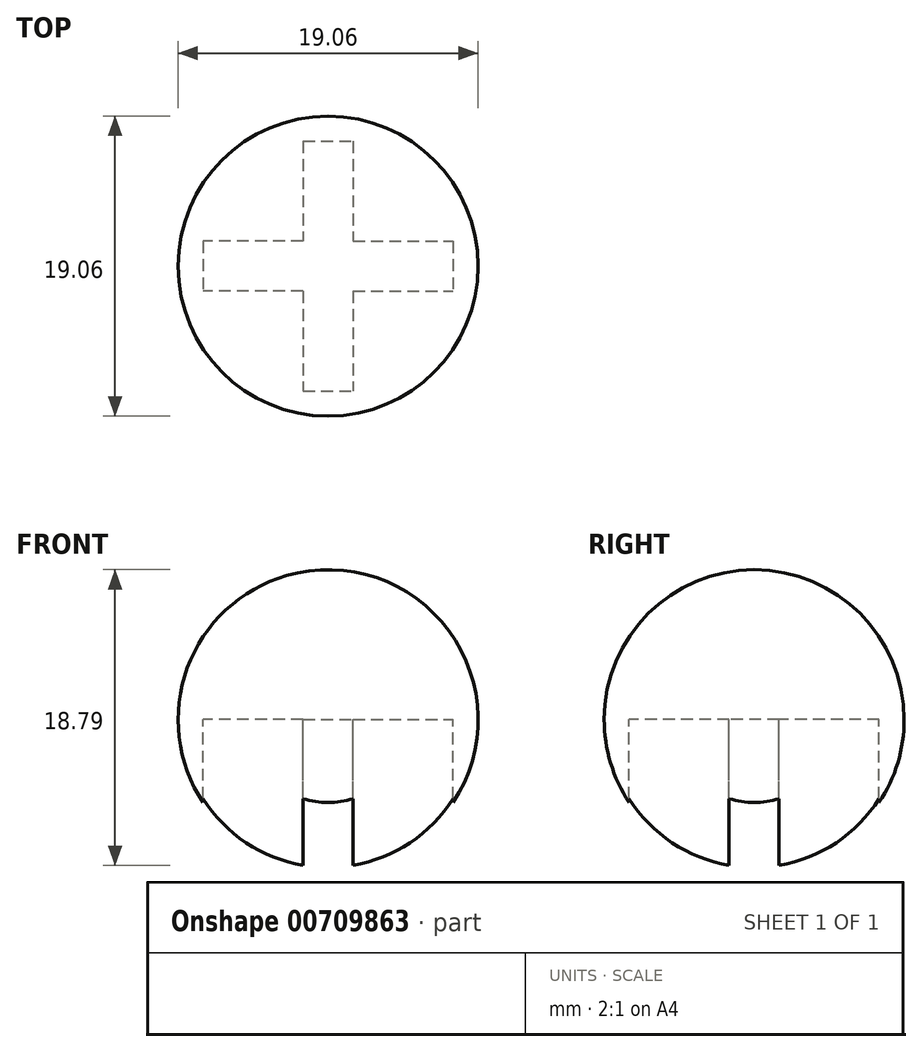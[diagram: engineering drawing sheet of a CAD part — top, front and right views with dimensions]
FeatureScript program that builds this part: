
annotation { "Feature Type Name" : "Feature", "Feature Type Description" : "" }
export const myFeature = defineFeature(function(context is Context, id is Id, definition is map)
    precondition{}
    {
        {
            var Q0;
            Q0=qCreatedBy(makeId("Top.planeOp"),FACE);
            var sketch = newSketch(context, id + "F0", { "sketchPlane" : qUnion([Q0])});
            skLineSegment(sketch, "E0", {"start": v(0, 9.53) * mm, "end": v(0, -9.53) * mm});
            skArc(sketch, "E1", {"start": v(0, -9.53) * mm, "mid": v(9.53, 0) * mm, "end": v(0, 9.53) * mm});
            skSolve(sketch);
        }
        {
            var Q0;
            Q0 = qSketchRegion(id + "F0", true);
            var Q1;
            Q1=sQuery(id+"F0.wireOp",EDGE,"E0");
            revolve(context, id + "F1", {"surfaceOperationType" : NewSurfaceOperationType.NEW, "entities" : qUnion([Q0]), "axis" : qUnion([Q1]), "revolveType" : RevolveType.FULL});
        }
        {
            var Q0;
            Q0=qCreatedBy(makeId("Top.planeOp"),FACE);
            var sketch = newSketch(context, id + "F2", { "sketchPlane" : qUnion([Q0])});
            skLineSegment(sketch, "E2.bottom", {"start": v(-1.59, 7.94) * mm, "end": v(1.59, 7.94) * mm});
            skLineSegment(sketch, "E2.top", {"start": v(-1.59, 1.59) * mm, "end": v(1.59, 1.59) * mm});
            skLineSegment(sketch, "E2.left", {"start": v(-1.59, 7.94) * mm, "end": v(-1.59, 1.59) * mm});
            skLineSegment(sketch, "E2.right", {"start": v(1.59, 7.94) * mm, "end": v(1.59, 1.59) * mm});
            skLineSegment(sketch, "E3.bottom", {"start": v(-1.59, -1.59) * mm, "end": v(1.59, -1.59) * mm});
            skLineSegment(sketch, "E3.top", {"start": v(-1.59, -7.94) * mm, "end": v(1.59, -7.94) * mm});
            skLineSegment(sketch, "E3.left", {"start": v(-1.59, -1.59) * mm, "end": v(-1.59, -7.94) * mm});
            skLineSegment(sketch, "E3.right", {"start": v(1.59, -1.59) * mm, "end": v(1.59, -7.94) * mm});
            skLineSegment(sketch, "E4.bottom", {"start": v(1.59, 1.59) * mm, "end": v(7.94, 1.59) * mm});
            skLineSegment(sketch, "E4.top", {"start": v(1.59, -1.59) * mm, "end": v(7.94, -1.59) * mm});
            skLineSegment(sketch, "E4.left", {"start": v(1.59, 1.59) * mm, "end": v(1.59, -1.59) * mm});
            skLineSegment(sketch, "E4.right", {"start": v(7.94, 1.59) * mm, "end": v(7.94, -1.59) * mm});
            skLineSegment(sketch, "E5.bottom", {"start": v(-1.59, 1.59) * mm, "end": v(-7.94, 1.59) * mm});
            skLineSegment(sketch, "E5.top", {"start": v(-1.59, -1.59) * mm, "end": v(-7.94, -1.59) * mm});
            skLineSegment(sketch, "E5.left", {"start": v(-1.59, 1.59) * mm, "end": v(-1.59, -1.59) * mm});
            skLineSegment(sketch, "E5.right", {"start": v(-7.94, 1.59) * mm, "end": v(-7.94, -1.59) * mm});
            skSolve(sketch);
        }
        {
            var Q0;
            Q0 = qSketchRegion(id + "F2", true);
            extrude(context, id + "F3", {"entities" : qUnion([Q0]), "operationType" : NewBodyOperationType.REMOVE, "oppositeDirection" : true, "depth" : 12.7 * mm, "offsetDistance" : 25.4 * mm});
        }
    });
